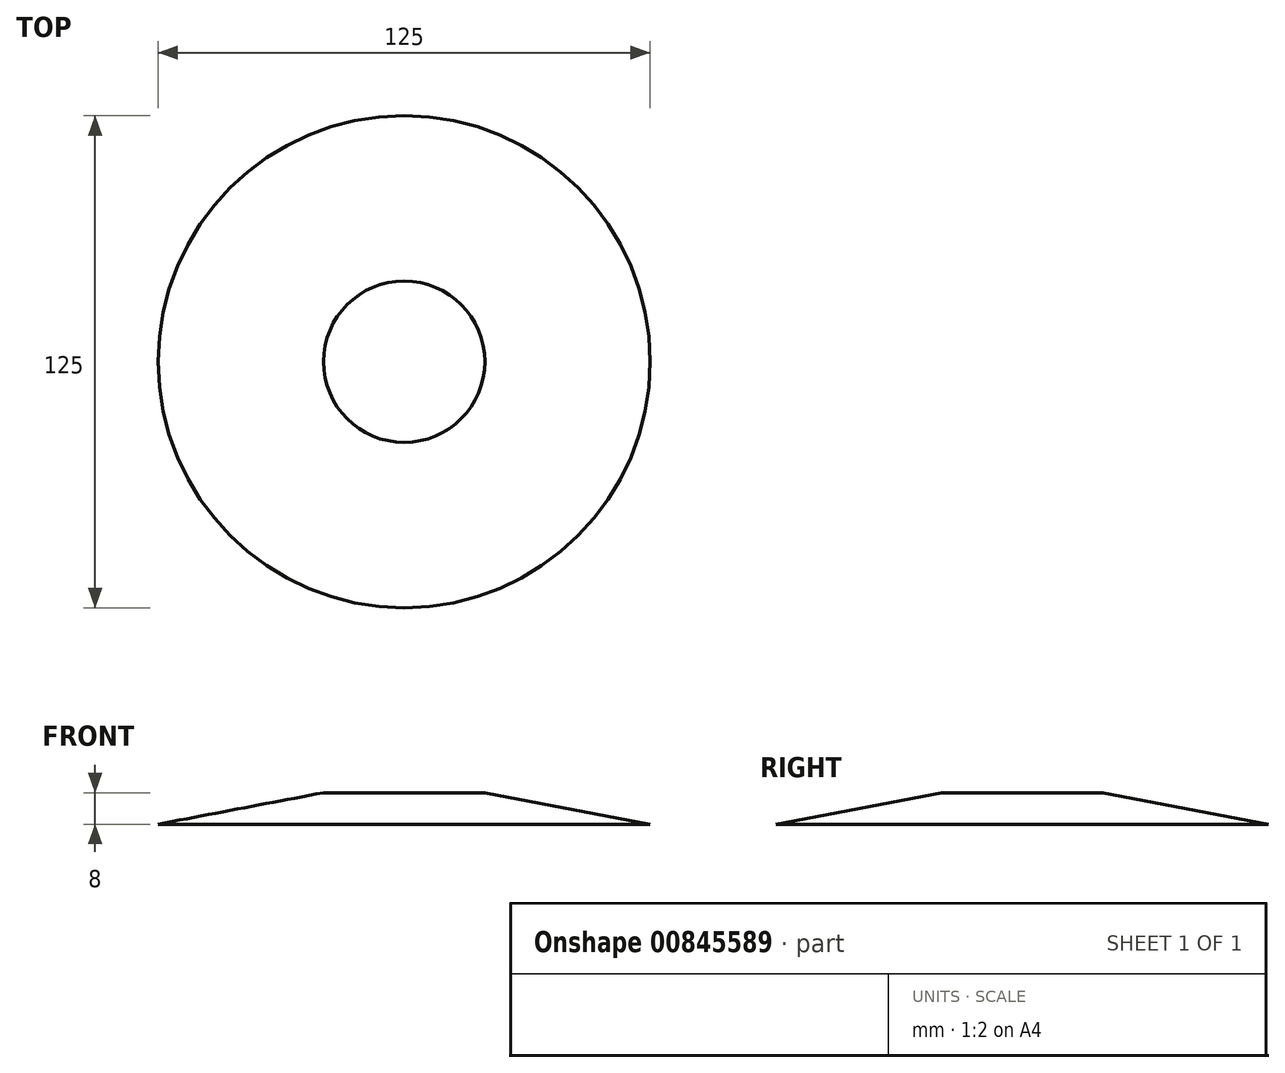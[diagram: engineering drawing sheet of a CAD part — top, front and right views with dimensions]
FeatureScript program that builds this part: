
annotation { "Feature Type Name" : "Feature", "Feature Type Description" : "" }
export const myFeature = defineFeature(function(context is Context, id is Id, definition is map)
    precondition{}
    {
        {
            var Q0;
            Q0=qCreatedBy(makeId("Front.planeOp"),FACE);
            var sketch = newSketch(context, id + "F0", { "sketchPlane" : qUnion([Q0])});
            skLineSegment(sketch, "E0", {"start": v(-62.5, 0) * mm, "end": v(-20.5, 8) * mm});
            skLineSegment(sketch, "E1", {"start": v(0, 65.23) * mm, "end": v(0, -58.86) * mm, "construction": true});
            skSolve(sketch);
        }
        {
            var Q0;
            Q0=sQuery(id+"F0.wireOp",EDGE,"E0");
            var Q1;
            Q1=sQuery(id+"F0.wireOp",EDGE,"VjlL5Pbp-V9Xs-Rt08-NaDS-mH0GXd1lubRQ");
            var Q2;
            Q2=sQuery(id+"F0.wireOp",EDGE,"E1");
            revolve(context, id + "F1", {"bodyType" : ToolBodyType.SURFACE, "surfaceOperationType" : NewSurfaceOperationType.NEW, "surfaceEntities" : qUnion([Q0, Q1]), "axis" : qUnion([Q2]), "revolveType" : RevolveType.FULL});
        }
    });
